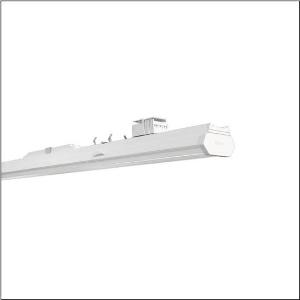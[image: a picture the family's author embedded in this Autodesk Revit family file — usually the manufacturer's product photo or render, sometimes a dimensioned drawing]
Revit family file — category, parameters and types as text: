
# Revit family: licross_11_protected_ho_51td11cn4exs
name_source: partatom
category: Lighting Fixtures
units: mm (PartAtom-declared; Revit-internal decimal feet)

## family parameters
Cut with Voids When Loaded = No
Host = Face
Light Source = No
Part Type = Normal
Room Calculation Point = No
Round Connector Dimension = Use Diameter
Shared = No

## types (1)
- --- (1 x LED, 14460 lm, 77.6 W, 4000K)
    Apparent Load = 78 VA
    CIE Flux Codes = 84 94 98 99 100
    Color Rendering = 80
    Color Temperature = 4000K
    Default Elevation = 1800 mm
    Description = Licross 11 Protected HO, luminaire insert, of sheet steel, galvanised, coil coated, white, length: 1.500mm, width: 90mm, height: 101mm, LED rated luminous flux: 14.460lm, light colour: 840, SDCM (Standard Deviation of Colour Matching)MacAdam ≤ 2 SDCM (initial), control gear: ON/OFF Multilumen, CLOi, with plug, 3-pole, with phase selection, mains connection: 220..240V, AC, 50/60Hz, start of lifetime: 78W, end of service life: 87W, internal wiring halogen-free, primary light control with lens, of plastic, primary optical cover: cover, of PMMA, light emission: direct distribution, primary light characteristic: symmetric, protection rating (complete): IP54, insulation class (complete): insulation class I (protective earthing), certification: CE, ENEC, VDE, UKCA, protection symbol: D if used in an environment with non-conductive dust loads with corresponding accessories, impact resistance: IK06, permissible ambient temperature for indoor applications: -35..+35°C, corresponds to IFS (International Featured Standards) requirements for safety and quality in the food industry, reducing of maximum allowable ambient temperature of 5°C with ceiling mounting, LABS conformity tested according to VDMA 24364:2018-05, The light source and the operating device comply with the requirements of the Ecodesign Regulation (EU) 2019/2020 and are replaceable in accordance with this regulation, packaging unit: 1 piece
    Height = 92 mm
    Lamp = 1 x LED
    Lamp Light Flux = 14460 lm
    Lamp Power = 77.6 W
    Lamp count = 1
    Length = 1500 mm
    Luminous efficacy = 186 lm/W
    Manufacturer = Siteco
    ModVariant = No
    Model = 51TD11CN4EXS
    Mounting Place = Ceiling
    Mounting Type = Pendant
    Number of Poles = 1
    OnlyDefault = Yes
    Power Factor = 1
    Product Name = Licross 11 Protected HO
    Product group = luminaire insert | ceiling pendant
    ProductGroupID = 901
    Protection Class = Protection class I
    Protection Degree = IP 54
    RLX_Detail_Level = 1
    RLX_Emergency_Light_Flux = 0 lm
    RLX_Emergency_Type = 0
    RLX_Emergency_Type_DB = No
    RlxData = <blob elided: 22377 chars, md5=76ce514a>
    Socket = socket
    Standby Power = 0 W
    System Light Flux = 14460 lm
    System Power = 78 W
    Type Comments = factory setting: luminous flux: 100 % | (A | C | E) | 181 mA
    Type Image = l_1256145.jpg
    URL = http://relux.com
    VarID = @adj_000713
    Voltage = 0 V
    Weight = 0.00 kg
    Width = 88 mm

## geometry (parser evidence)
native form markers: Blend x4, Sweep x10
no freeform markers — native parametric forms only
